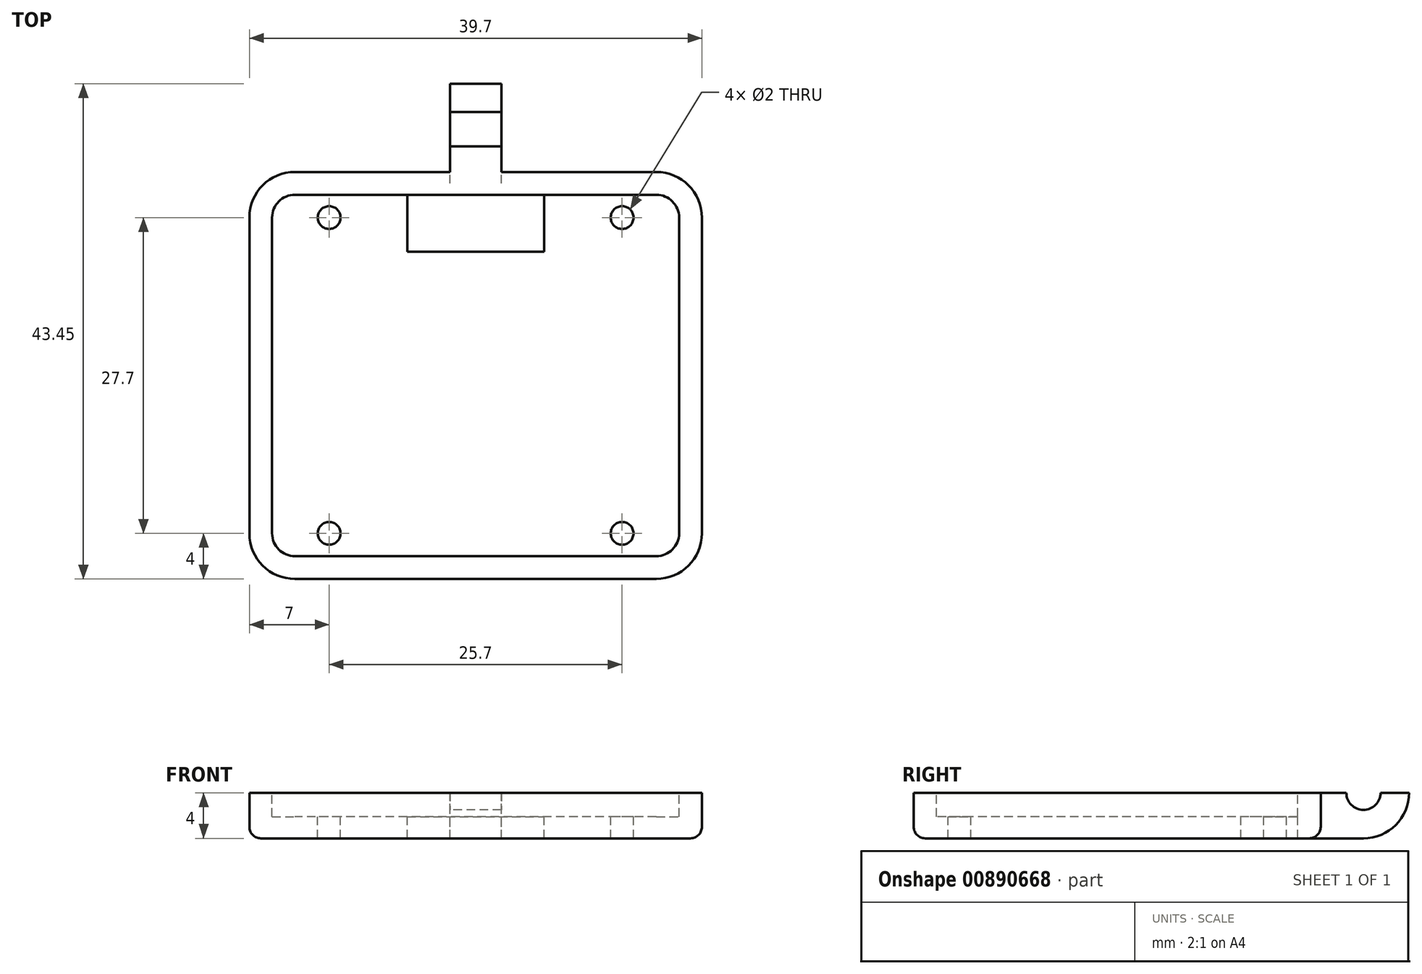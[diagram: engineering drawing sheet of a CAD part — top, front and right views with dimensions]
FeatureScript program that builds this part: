
annotation { "Feature Type Name" : "Feature", "Feature Type Description" : "" }
export const myFeature = defineFeature(function(context is Context, id is Id, definition is map)
    precondition{}
    {
        {
            var Q0;
            Q0=qCreatedBy(makeId("Top.planeOp"),FACE);
            var sketch = newSketch(context, id + "F0", { "sketchPlane" : qUnion([Q0])});
            skLineSegment(sketch, "E0.bottom", {"start": v(15.85, 15.85) * mm, "end": v(-15.85, 15.85) * mm, "construction": true});
            skLineSegment(sketch, "E0.top", {"start": v(15.85, -15.85) * mm, "end": v(-15.85, -15.85) * mm, "construction": true});
            skLineSegment(sketch, "E0.left", {"start": v(17.85, 13.85) * mm, "end": v(17.85, -13.85) * mm, "construction": true});
            skLineSegment(sketch, "E0.right", {"start": v(-17.85, 13.85) * mm, "end": v(-17.85, -13.85) * mm, "construction": true});
            skPoint(sketch, "E1.visualSharp", {"position": v(-17.85, 15.85) * mm});
            skArc(sketch, "E1.filletArc", {"start": v(-15.85, 15.85) * mm, "mid": v(-17.26, 15.26) * mm, "end": v(-17.85, 13.85) * mm, "construction": true});
            skPoint(sketch, "E2.visualSharp", {"position": v(-17.85, -15.85) * mm});
            skArc(sketch, "E2.filletArc", {"start": v(-17.85, -13.85) * mm, "mid": v(-17.26, -15.26) * mm, "end": v(-15.85, -15.85) * mm, "construction": true});
            skPoint(sketch, "E3.visualSharp", {"position": v(17.85, -15.85) * mm});
            skArc(sketch, "E3.filletArc", {"start": v(15.85, -15.85) * mm, "mid": v(17.26, -15.26) * mm, "end": v(17.85, -13.85) * mm, "construction": true});
            skPoint(sketch, "E4.visualSharp", {"position": v(17.85, 15.85) * mm});
            skArc(sketch, "E4.filletArc", {"start": v(17.85, 13.85) * mm, "mid": v(17.26, 15.26) * mm, "end": v(15.85, 15.85) * mm, "construction": true});
            skArc(sketch, "E5.0", {"start": v(19.85, 13.85) * mm, "mid": v(18.68, 16.68) * mm, "end": v(15.85, 17.85) * mm});
            skLineSegment(sketch, "E5.1", {"start": v(15.85, 17.85) * mm, "end": v(-15.85, 17.85) * mm});
            skLineSegment(sketch, "E5.2", {"start": v(19.85, 13.85) * mm, "end": v(19.85, -13.85) * mm});
            skArc(sketch, "E5.3", {"start": v(-15.85, 17.85) * mm, "mid": v(-18.68, 16.68) * mm, "end": v(-19.85, 13.85) * mm});
            skArc(sketch, "E5.4", {"start": v(15.85, -17.85) * mm, "mid": v(18.68, -16.68) * mm, "end": v(19.85, -13.85) * mm});
            skLineSegment(sketch, "E5.5", {"start": v(15.85, -17.85) * mm, "end": v(-15.85, -17.85) * mm});
            skArc(sketch, "E5.6", {"start": v(-19.85, -13.85) * mm, "mid": v(-18.68, -16.68) * mm, "end": v(-15.85, -17.85) * mm});
            skLineSegment(sketch, "E5.7", {"start": v(-19.85, 13.85) * mm, "end": v(-19.85, -13.85) * mm});
            skSolve(sketch);
        }
        {
            var Q0;
            Q0=makeQuery(id+"F0.imprint","IMPRINT",FACE,{"disambiguationData":[TD([[makeQuery(id+"F0.imprint","IMPRINT",EDGE,{"derivedFrom":sQuery(id+"F0.wireOp",EDGE,"E5.0")}),1.0]])]});
            extrude(context, id + "F1", {"entities" : qUnion([Q0]), "depth" : 4 * mm, "offsetDistance" : 25 * mm});
        }
        {
            var Q0;
            Q0=makeQuery(id+"F1.opExtrude","CAP_FACE",FACE,{"disambiguationData":[OSD([sQuery(id+"F0.wireOp",EDGE,"E5.0"),sQuery(id+"F0.wireOp",EDGE,"E5.1"),sQuery(id+"F0.wireOp",EDGE,"E5.2"),sQuery(id+"F0.wireOp",EDGE,"E5.3"),sQuery(id+"F0.wireOp",EDGE,"E5.4"),sQuery(id+"F0.wireOp",EDGE,"E5.5"),sQuery(id+"F0.wireOp",EDGE,"E5.6"),sQuery(id+"F0.wireOp",EDGE,"E5.7")])],"isStart":false});
            var sketch = newSketch(context, id + "F2", { "sketchPlane" : qUnion([Q0])});
            skLineSegment(sketch, "E6.bottom", {"start": v(15.85, 15.85) * mm, "end": v(-15.85, 15.85) * mm});
            skLineSegment(sketch, "E6.top", {"start": v(15.85, -15.85) * mm, "end": v(-15.85, -15.85) * mm});
            skLineSegment(sketch, "E6.left", {"start": v(17.85, 13.85) * mm, "end": v(17.85, -13.85) * mm});
            skLineSegment(sketch, "E6.right", {"start": v(-17.85, 13.85) * mm, "end": v(-17.85, -13.85) * mm});
            skPoint(sketch, "E7.visualSharp", {"position": v(-17.85, 15.85) * mm});
            skArc(sketch, "E7.filletArc", {"start": v(-15.85, 15.85) * mm, "mid": v(-17.26, 15.26) * mm, "end": v(-17.85, 13.85) * mm});
            skPoint(sketch, "E8.visualSharp", {"position": v(-17.85, -15.85) * mm});
            skArc(sketch, "E8.filletArc", {"start": v(-17.85, -13.85) * mm, "mid": v(-17.26, -15.26) * mm, "end": v(-15.85, -15.85) * mm});
            skPoint(sketch, "E9.visualSharp", {"position": v(17.85, -15.85) * mm});
            skArc(sketch, "E9.filletArc", {"start": v(15.85, -15.85) * mm, "mid": v(17.26, -15.26) * mm, "end": v(17.85, -13.85) * mm});
            skPoint(sketch, "E10.visualSharp", {"position": v(17.85, 15.85) * mm});
            skArc(sketch, "E10.filletArc", {"start": v(17.85, 13.85) * mm, "mid": v(17.26, 15.26) * mm, "end": v(15.85, 15.85) * mm});
            skSolve(sketch);
        }
        {
            var Q0;
            Q0 = qSketchRegion(id + "F2", true);
            extrude(context, id + "F3", {"entities" : qUnion([Q0]), "operationType" : NewBodyOperationType.REMOVE, "oppositeDirection" : true, "depth" : 2.1 * mm, "offsetDistance" : 25 * mm});
        }
        {
            var Q0;
            Q0=qCreatedBy(makeId("Right.planeOp"),FACE);
            var sketch = newSketch(context, id + "F4", { "sketchPlane" : qUnion([Q0])});
            skArc(sketch, "E11", {"start": v(21.6, 0) * mm, "mid": v(24.43, 1.17) * mm, "end": v(25.6, 4) * mm});
            skLineSegment(sketch, "E12.0", {"start": v(17.85, 4) * mm, "end": v(17.85, 0) * mm});
            skLineSegment(sketch, "E13", {"start": v(17.85, 0) * mm, "end": v(21.6, 0) * mm});
            skArc(sketch, "E14", {"start": v(20.1, 4) * mm, "mid": v(21.6, 2.5) * mm, "end": v(23.1, 4) * mm});
            skLineSegment(sketch, "E15", {"start": v(17.6, 4) * mm, "end": v(21.6, 4) * mm});
            skLineSegment(sketch, "E16.trimOffspring", {"start": v(23.1, 4) * mm, "end": v(25.6, 4) * mm});
            skLineSegment(sketch, "E17", {"start": v(17.85, 4) * mm, "end": v(15.85, 4) * mm});
            skLineSegment(sketch, "E18", {"start": v(15.85, 4) * mm, "end": v(15.85, 0) * mm});
            skLineSegment(sketch, "E19", {"start": v(15.85, 0) * mm, "end": v(17.85, 0) * mm});
            skSolve(sketch);
        }
        {
            var Q0;
            Q0 = qSketchRegion(id + "F4", true);
            extrude(context, id + "F5", {"entities" : qUnion([Q0]), "operationType" : NewBodyOperationType.ADD, "depth" : 2.25 * mm, "offsetDistance" : 25 * mm, "hasSecondDirection" : true, "secondDirectionOppositeDirection" : true, "secondDirectionDepth" : 2.25 * mm});
        }
        {
            var Q0;
            Q0=makeQuery(id+"F3.boolean.opBoolean","COPY",FACE,{"derivedFrom":makeQuery(id+"F3.opExtrude","CAP_FACE",FACE,{"disambiguationData":[OSD([sQuery(id+"F2.wireOp",EDGE,"E6.bottom"),sQuery(id+"F2.wireOp",EDGE,"E6.top"),sQuery(id+"F2.wireOp",EDGE,"E6.left"),sQuery(id+"F2.wireOp",EDGE,"E6.right"),sQuery(id+"F2.wireOp",EDGE,"E7.filletArc"),sQuery(id+"F2.wireOp",EDGE,"E8.filletArc"),sQuery(id+"F2.wireOp",EDGE,"E9.filletArc"),sQuery(id+"F2.wireOp",EDGE,"E10.filletArc")])],"isStart":false})});
            var sketch = newSketch(context, id + "F6", { "sketchPlane" : qUnion([Q0])});
            skLineSegment(sketch, "E20.bottom", {"start": v(-6, 15.85) * mm, "end": v(6, 15.85) * mm});
            skLineSegment(sketch, "E20.top", {"start": v(-6, 10.85) * mm, "end": v(6, 10.85) * mm});
            skLineSegment(sketch, "E20.left", {"start": v(-6, 15.85) * mm, "end": v(-6, 10.85) * mm});
            skLineSegment(sketch, "E20.right", {"start": v(6, 15.85) * mm, "end": v(6, 10.85) * mm});
            skCircle(sketch, "E21", {"center": v(-12.85, 13.85) * mm, "radius": 1 * mm});
            skCircle(sketch, "E22", {"center": v(12.85, 13.85) * mm, "radius": 1 * mm});
            skCircle(sketch, "E23", {"center": v(-12.85, -13.85) * mm, "radius": 1 * mm});
            skCircle(sketch, "E24", {"center": v(12.85, -13.85) * mm, "radius": 1 * mm});
            skSolve(sketch);
        }
        {
            var Q0;
            Q0 = qSketchRegion(id + "F6", true);
            extrude(context, id + "F7", {"entities" : qUnion([Q0]), "operationType" : NewBodyOperationType.REMOVE, "oppositeDirection" : true, "depth" : 25 * mm, "offsetDistance" : 25 * mm});
        }
        {
            var Q0;
            Q0=makeQuery(id+"F1.opExtrude","CAP_EDGE",EDGE,{"disambiguationData":[OSD([sQuery(id+"F0.wireOp",EDGE,"E5.7")])],"isStart":true});
            fillet(context, id + "F8", {"entities" : qUnion([Q0]), "radius" : 1 * mm, "tangentPropagation" : true, "allowEdgeOverflow" : false});
        }
    });
